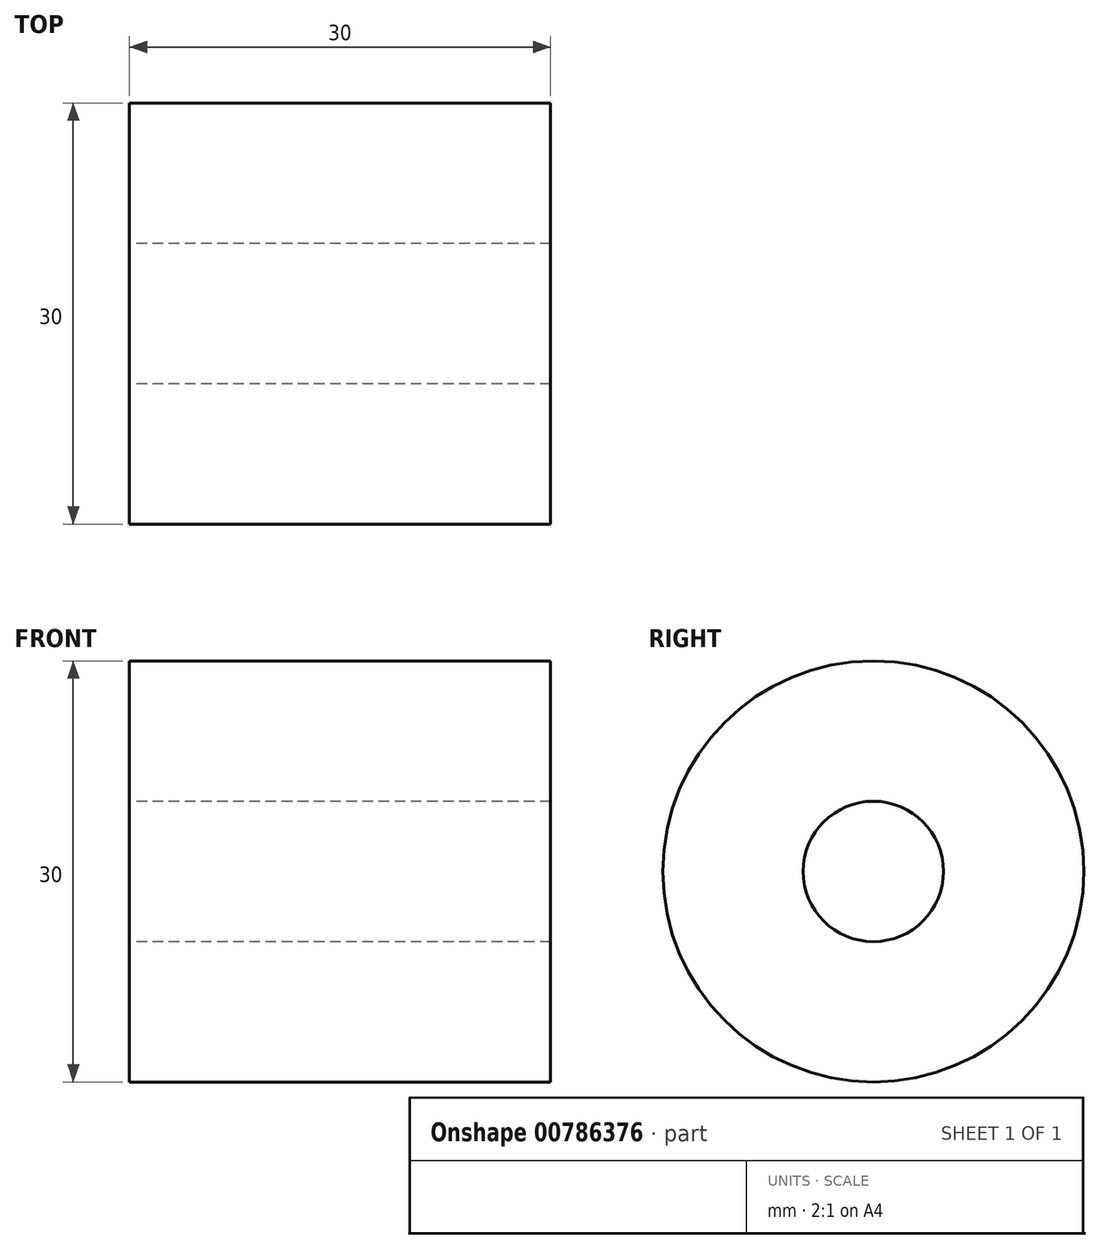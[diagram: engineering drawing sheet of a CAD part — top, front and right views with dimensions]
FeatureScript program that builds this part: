
annotation { "Feature Type Name" : "Feature", "Feature Type Description" : "" }
export const myFeature = defineFeature(function(context is Context, id is Id, definition is map)
    precondition{}
    {
        {
            var Q0;
            Q0=qCreatedBy(makeId("Right.planeOp"),FACE);
            var sketch = newSketch(context, id + "F0", { "sketchPlane" : qUnion([Q0])});
            skCircle(sketch, "E0", {"center": v(0, 0) * mm, "radius": 15 * mm});
            skCircle(sketch, "E1.0", {"center": v(0, 0) * mm, "radius": 5 * mm});
            skSolve(sketch);
        }
        {
            var Q0;
            Q0=makeQuery(id+"F0.imprint","IMPRINT",FACE,{"disambiguationData":[TD([[makeQuery(id+"F0.imprint","IMPRINT",EDGE,{"derivedFrom":sQuery(id+"F0.wireOp",EDGE,"E0")}),1.0]])]});
            extrude(context, id + "F1", {"entities" : qUnion([Q0]), "depth" : 30 * mm, "offsetDistance" : 25 * mm});
        }
    });
